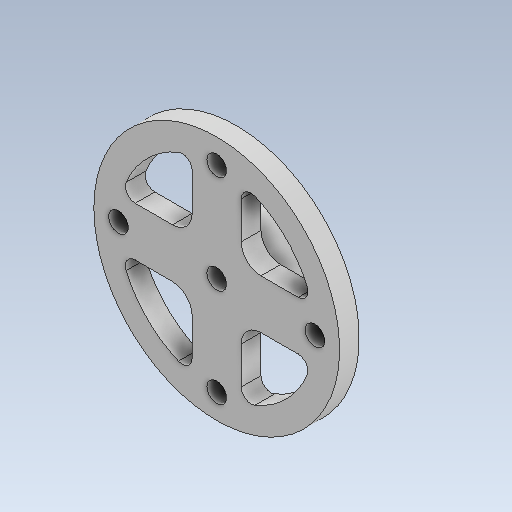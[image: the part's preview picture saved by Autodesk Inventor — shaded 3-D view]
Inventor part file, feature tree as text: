
AUTODESK INVENTOR PART (.ipt)
format: ipt  version: 2020 (Build 240168000, 168)  size: 197,120 bytes
history: native  units: mm
features: sketch x5, other x3
ambient origin geometry x8: Origin, YZ Plane, XZ Plane, XY Plane, X Axis, Y Axis, Z Axis, Center Point
bodies: Solid1 (feature_tree)
feature tree (8):
  other  "tendon_wh_1.ipt"
  other  "Solid1::tendon_wh_1.ipt"
  other  "TaggingFeature1"
  sketch  "Sketch1"  dims[d0=10.0mm]
  sketch  "Sketch2"
  sketch  "Sketch3"
  sketch  "Sketch4"
  sketch  "Sketch5"
